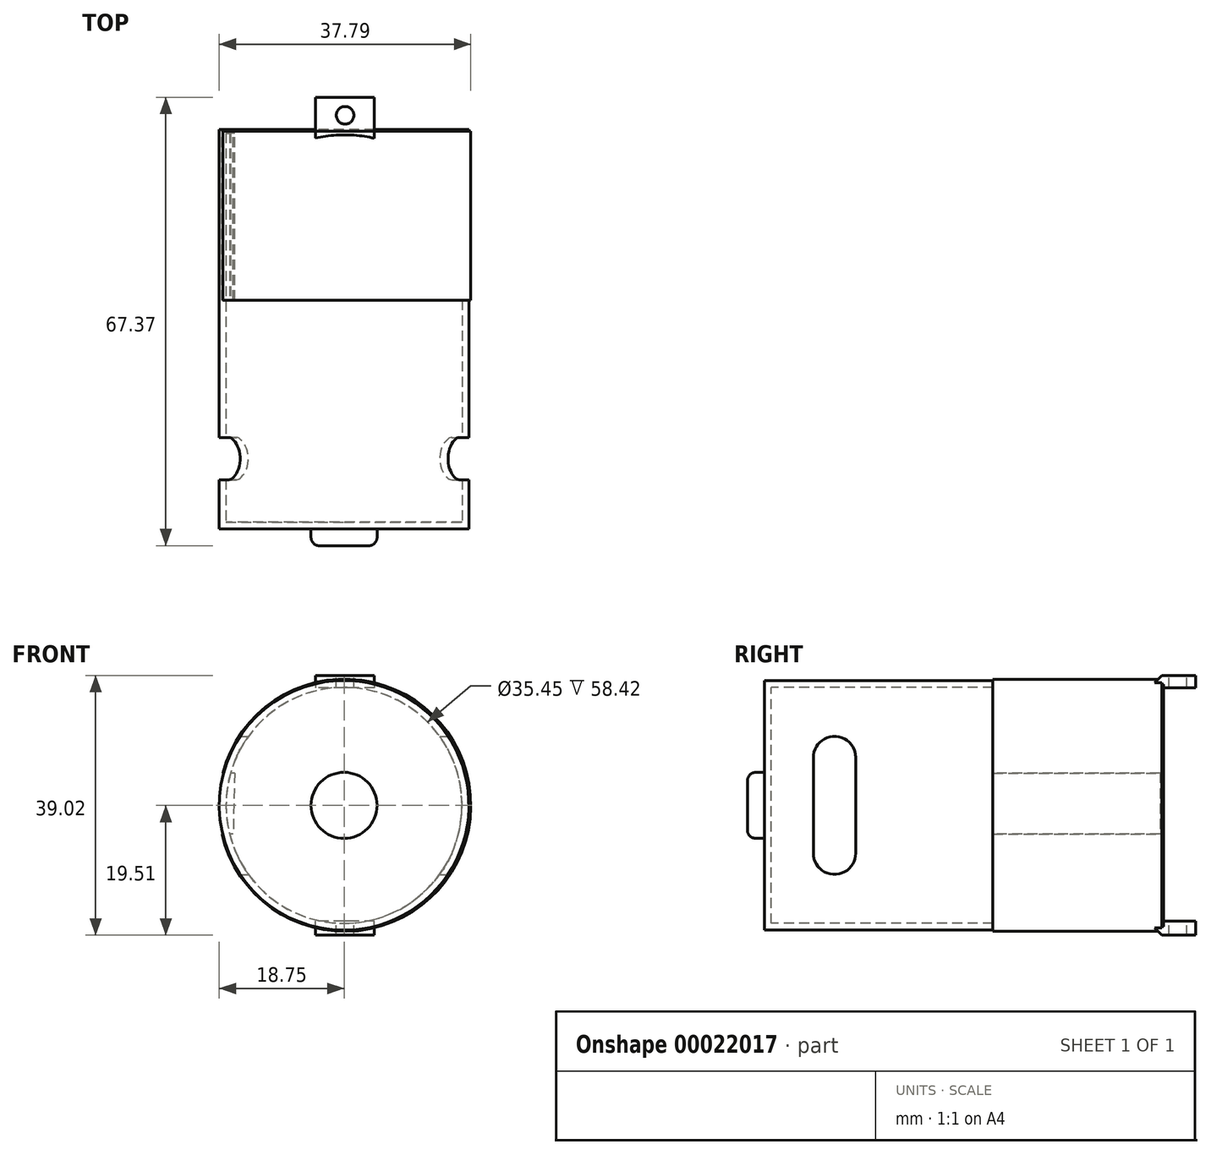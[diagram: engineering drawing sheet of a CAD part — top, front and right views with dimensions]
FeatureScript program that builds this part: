
annotation { "Feature Type Name" : "Feature", "Feature Type Description" : "" }
export const myFeature = defineFeature(function(context is Context, id is Id, definition is map)
    precondition{}
    {
        {
            var Q0;
            Q0=qCreatedBy(makeId("Front.planeOp"),FACE);
            var sketch = newSketch(context, id + "F0", { "sketchPlane" : qUnion([Q0])});
            skCircle(sketch, "E0", {"center": v(0, 0) * mm, "radius": 18.75 * mm});
            skSolve(sketch);
        }
        {
            var Q0;
            Q0 = qSketchRegion(id + "F0", true);
            extrude(context, id + "F1", {"entities" : qUnion([Q0]), "depth" : 60 * mm});
        }
        {
            var Q0;
            Q0=qCreatedBy(makeId("Right.planeOp"),FACE);
            cPlane(context, id + "F2", {"entities" : qUnion([Q0]), "cplaneType" : CPlaneType.OFFSET, "offset" : 19.05 * mm, "width" : 152.4 * mm, "height" : 152.4 * mm});
        }
        {
            var Q0;
            Q0=qCreatedBy(id+"F2.planeOp",FACE);
            var sketch = newSketch(context, id + "F3", { "sketchPlane" : qUnion([Q0])});
            skArc(sketch, "E1", {"start": v(-52.63, -7.2) * mm, "mid": v(-49.45, -10.38) * mm, "end": v(-46.28, -7.2) * mm});
            skLineSegment(sketch, "E2", {"start": v(-52.63, -7.2) * mm, "end": v(-46.28, -7.2) * mm});
            skLineSegment(sketch, "E3", {"start": v(-52.63, -7.2) * mm, "end": v(-52.63, 7.2) * mm});
            skLineSegment(sketch, "E4", {"start": v(-46.28, -7.2) * mm, "end": v(-46.28, 7.2) * mm});
            skArc(sketch, "E5", {"start": v(-46.28, 7.2) * mm, "mid": v(-49.45, 10.38) * mm, "end": v(-52.63, 7.2) * mm});
            skSolve(sketch);
        }
        {
            var Q0;
            Q0 = qSketchRegion(id + "F3", true);
            extrude(context, id + "F4", {"entities" : qUnion([Q0]), "operationType" : NewBodyOperationType.REMOVE, "oppositeDirection" : true, "depth" : 127 * mm});
        }
        {
            var Q0;
            Q0=makeQuery(id+"F1.opExtrude","CAP_FACE",FACE,{"disambiguationData":[OSD([sQuery(id+"F0.wireOp",EDGE,"E0")])],"isStart":false});
            var sketch = newSketch(context, id + "F5", { "sketchPlane" : qUnion([Q0])});
            skCircle(sketch, "E6", {"center": v(0, 0) * mm, "radius": 4.96 * mm});
            skSolve(sketch);
        }
        {
            var Q0;
            Q0 = qSketchRegion(id + "F5", true);
            extrude(context, id + "F6", {"entities" : qUnion([Q0]), "operationType" : NewBodyOperationType.ADD, "depth" : 2.54 * mm});
        }
        {
            var Q0;
            Q0=makeQuery(id+"F6.opExtrude","CAP_EDGE",EDGE,{"disambiguationData":[OSD([sQuery(id+"F5.wireOp",EDGE,"E6")])],"isStart":false});
            fillet(context, id + "F7", {"entities" : qUnion([Q0]), "radius" : 1.27 * mm, "tangentPropagation" : true, "allowEdgeOverflow" : false});
        }
        {
            var Q0;
            Q0=makeQuery(id+"F4.boolean.opBoolean","COPY",FACE,{"derivedFrom":makeQuery(id+"F4.opExtrude","SWEPT_FACE",FACE,{"disambiguationData":[OSD([sQuery(id+"F3.wireOp",EDGE,"E4")])]})});
            var sketch = newSketch(context, id + "F8", { "sketchPlane" : qUnion([Q0])});
            skCircle(sketch, "E7", {"center": v(0, 0) * mm, "radius": 17.72 * mm});
            skSolve(sketch);
        }
        {
            var Q0;
            Q0 = qSketchRegion(id + "F8", true);
            extrude(context, id + "F9", {"entities" : qUnion([Q0]), "operationType" : NewBodyOperationType.REMOVE, "oppositeDirection" : true, "depth" : 45.72 * mm, "hasSecondDirection" : true, "secondDirectionOppositeDirection" : false, "secondDirectionDepth" : 12.7 * mm});
        }
        {
            var Q0;
            Q0=makeQuery(id+"F1.opExtrude","CAP_FACE",FACE,{"disambiguationData":[OSD([sQuery(id+"F0.wireOp",EDGE,"E0")])],"isStart":true});
            cPlane(context, id + "F10", {"entities" : qUnion([Q0]), "cplaneType" : CPlaneType.OFFSET, "offset" : 0.25 * mm, "oppositeDirection" : true, "width" : 152.4 * mm, "height" : 152.4 * mm});
        }
        {
            var Q0;
            Q0=qCreatedBy(id+"F10.planeOp",FACE);
            var sketch = newSketch(context, id + "F11", { "sketchPlane" : qUnion([Q0])});
            skLineSegment(sketch, "E8.bottom", {"start": v(-4.57, 19.5) * mm, "end": v(4.26, 19.5) * mm});
            skLineSegment(sketch, "E8.top", {"start": v(-4.57, 17.67) * mm, "end": v(4.26, 17.67) * mm});
            skLineSegment(sketch, "E8.left", {"start": v(-4.57, 19.5) * mm, "end": v(-4.57, 17.67) * mm});
            skLineSegment(sketch, "E8.right", {"start": v(4.26, 19.5) * mm, "end": v(4.26, 17.67) * mm});
            skLineSegment(sketch, "E9.bottom", {"start": v(-4.57, -19.5) * mm, "end": v(4.26, -19.5) * mm});
            skLineSegment(sketch, "E9.top", {"start": v(-4.57, -17.42) * mm, "end": v(4.26, -17.42) * mm});
            skLineSegment(sketch, "E9.left", {"start": v(-4.57, -19.5) * mm, "end": v(-4.57, -17.42) * mm});
            skLineSegment(sketch, "E9.right", {"start": v(4.26, -19.5) * mm, "end": v(4.26, -17.42) * mm});
            skSolve(sketch);
        }
        {
            var Q0;
            Q0 = qSketchRegion(id + "F11", true);
            extrude(context, id + "F12", {"entities" : qUnion([Q0]), "operationType" : NewBodyOperationType.ADD, "depth" : 5.08 * mm, "hasSecondDirection" : true, "secondDirectionOppositeDirection" : true, "secondDirectionDepth" : 2.54 * mm});
        }
        {
            var Q0;
            Q0=makeQuery(id+"F12.opExtrude","SWEPT_FACE",FACE,{"disambiguationData":[OSD([sQuery(id+"F11.wireOp",EDGE,"E8.bottom")])]});
            var sketch = newSketch(context, id + "F13", { "sketchPlane" : qUnion([Q0])});
            skCircle(sketch, "E10", {"center": v(0.15, 2.13) * mm, "radius": 1.32 * mm});
            skPoint(sketch, "E10.centerSnap0", {"position": v(0.15, 4.83) * mm});
            skSolve(sketch);
        }
        {
            var Q0;
            Q0 = qSketchRegion(id + "F13", true);
            extrude(context, id + "F14", {"entities" : qUnion([Q0]), "operationType" : NewBodyOperationType.REMOVE, "oppositeDirection" : true, "depth" : 46.72 * mm});
        }
        {
            var Q0;
            Q0=makeQuery(id+"F12.opExtrude","CAP_EDGE",EDGE,{"disambiguationData":[OSD([sQuery(id+"F11.wireOp",EDGE,"E8.bottom")])],"isStart":true});
            var Q1;
            Q1=makeQuery(id+"F12.opExtrude","CAP_EDGE",EDGE,{"disambiguationData":[OSD([sQuery(id+"F11.wireOp",EDGE,"E9.bottom")])],"isStart":true});
            chamfer(context, id + "F15", {"entities" : qUnion([Q0, Q1]), "width" : 2.54 * mm, "tangentPropagation" : true});
        }
        {
            var Q0;
            Q0=qCreatedBy(id+"F10.planeOp",FACE);
            var sketch = newSketch(context, id + "F16", { "sketchPlane" : qUnion([Q0])});
            skArc(sketch, "E11", {"start": v(18.23, 4.85) * mm, "mid": v(-19.04, -0.24) * mm, "end": v(18.35, -4.32) * mm});
            skLineSegment(sketch, "E12", {"start": v(18.35, -4.32) * mm, "end": v(16.65, -4.32) * mm});
            skLineSegment(sketch, "E13", {"start": v(18.23, 4.85) * mm, "end": v(16.44, 4.85) * mm});
            skLineSegment(sketch, "E14", {"start": v(16.65, -4.32) * mm, "end": v(16.44, 4.85) * mm});
            skSolve(sketch);
        }
        {
            var Q0;
            Q0 = qSketchRegion(id + "F16", true);
            extrude(context, id + "F17", {"entities" : qUnion([Q0]), "operationType" : NewBodyOperationType.ADD, "oppositeDirection" : true, "depth" : 25.4 * mm});
        }
    });
